# Revit family: Hose_Box-Single_Temp-Acorn-818X-SSLF_Series.rfaxx
name_source: partatom
category: Plumbing Fixtures
units: mm (PartAtom-declared; Revit-internal decimal feet)

## family parameters
Cut with Voids When Loaded = Yes
Host = Face
OmniClass Number = 23.65.55.14
OmniClass Title = Valves for Liquid Services
Part Type = Normal
Room Calculation Point = No
Round Connector Dimension = Use Diameter
Shared = Yes

## types (2) — shared parameters
Assembly Code = D2010800
CW Connection = Yes
CWFU = 1
Default Elevation = 0"
Finish = Stainless Steel-Acorn-Polished Satin
HW Connection = No
IAPMO Compliance = CUPC certified by IAPMO for U.S. and Canada
Installation Instruction Link = https://www.acorneng.com
Installation Type = Wall Mounted
Manufacturer = Acorn
Material = Stainless Steel-Acorn-Polished Satin
NPT Connection Diameter = 3/4"
Price = Prices may vary. Please consult Manufacturer Representative for most up-to-date price list.
Product Documentation Link = https://www.acorneng.com
Product Page URL = https://www.acorneng.com
URL = https://www.acorneng.com
Vent Connection = No
WFU = 1.5
Waste Connection = Yes
Waste Connection Diameter = 2"
Width = 10 1/2"
cUPC Compliant = Yes
zero-valued in all types: HWFU

## per-type parameters (varying)
| type | 8180-SSLF Single Temperature Less Vacuum Breaker | 8181-SSLF Single Temperature With Vacuum Breaker | Description |
| 8181-SSLF | No | Yes | Single Temp Stainless Steel Hose Box with Waste Outlet and Vacuum Breaker |
| 8180-SSLF | Yes | No | Single Temp Stainless Steel Hose Box with Waste Outlet |

note: column(s) folded — value = type name in every type: Model

## geometry (parser evidence)
native form markers: Sweep x2
no freeform markers — native parametric forms only
